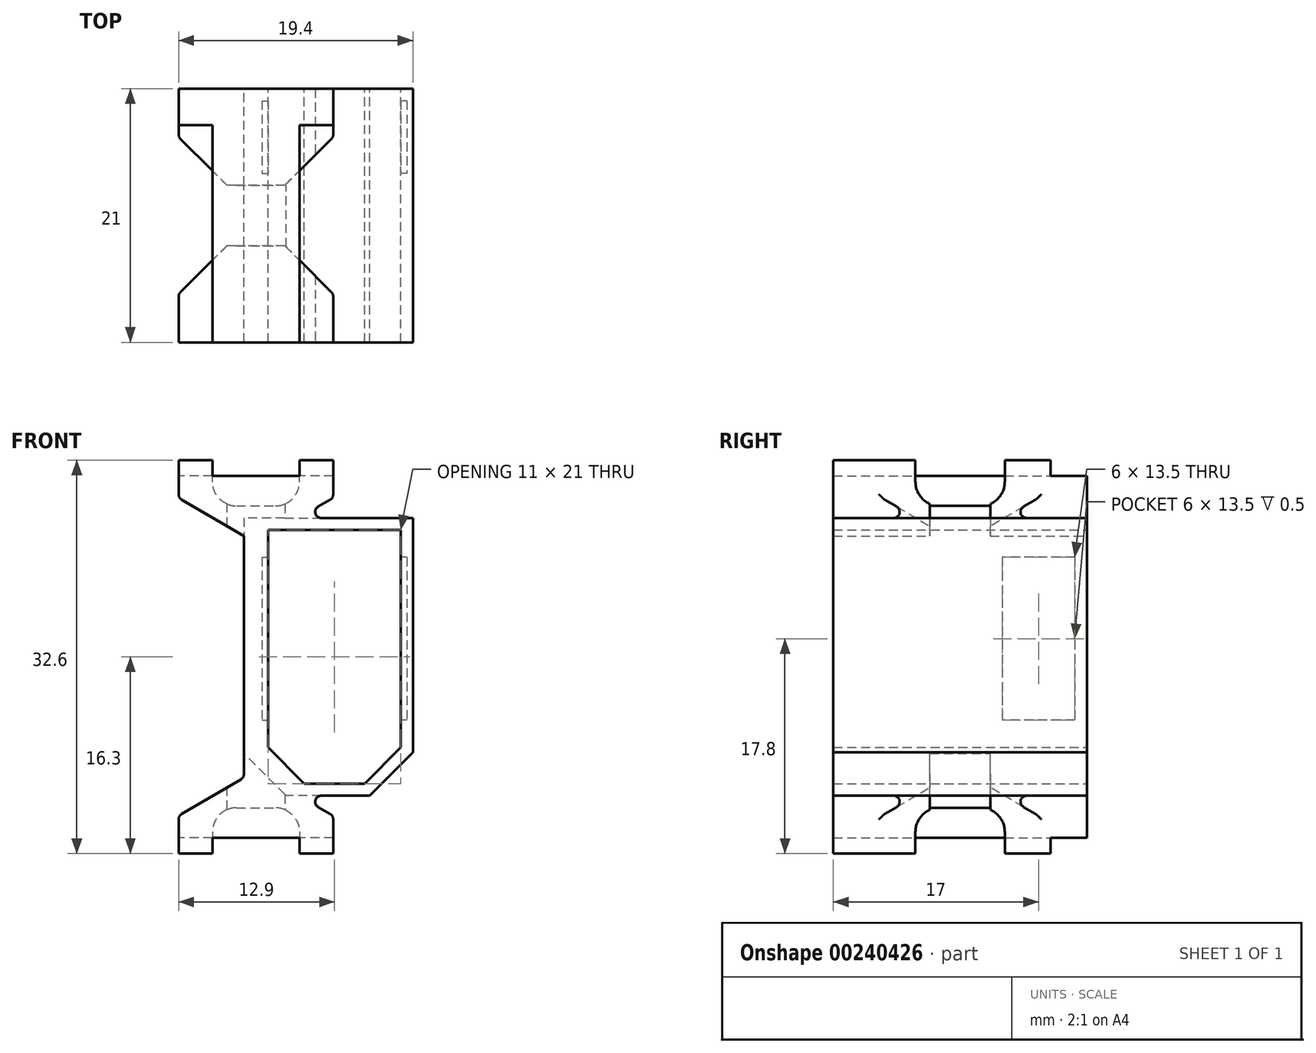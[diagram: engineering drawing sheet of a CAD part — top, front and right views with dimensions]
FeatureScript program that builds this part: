
annotation { "Feature Type Name" : "Feature", "Feature Type Description" : "" }
export const myFeature = defineFeature(function(context is Context, id is Id, definition is map)
    precondition{}
    {
        {
            var Q0;
            Q0=qCreatedBy(makeId("Front.planeOp"),FACE);
            var sketch = newSketch(context, id + "F0", { "sketchPlane" : qUnion([Q0])});
            skLineSegment(sketch, "E0", {"start": v(-1, 10) * mm, "end": v(-1, -10) * mm});
            skLineSegment(sketch, "E1", {"start": v(-6.4, 16.3) * mm, "end": v(-6.4, 13.16) * mm});
            skLineSegment(sketch, "E2", {"start": v(-6.4, 16.3) * mm, "end": v(-3.6, 16.3) * mm});
            skLineSegment(sketch, "E3", {"start": v(-3.6, 16.3) * mm, "end": v(-3.6, 15) * mm});
            skLineSegment(sketch, "E4", {"start": v(-3.6, 15) * mm, "end": v(0, 15) * mm});
            skLineSegment(sketch, "E5", {"start": v(-6.4, 13.16) * mm, "end": v(-1, 10) * mm});
            skLineSegment(sketch, "E6.MirrorCS", {"start": v(-3.6, -16.3) * mm, "end": v(-3.6, -15) * mm});
            skLineSegment(sketch, "E7.MirrorCS", {"start": v(-6.4, -13.16) * mm, "end": v(-1, -10) * mm});
            skLineSegment(sketch, "E8.MirrorCS", {"start": v(-3.6, -15) * mm, "end": v(0, -15) * mm});
            skLineSegment(sketch, "E9.MirrorCS", {"start": v(-6.4, -16.3) * mm, "end": v(-6.4, -13.16) * mm});
            skLineSegment(sketch, "E10.MirrorCS", {"start": v(-6.4, -16.3) * mm, "end": v(-3.6, -16.3) * mm});
            skLineSegment(sketch, "E11.MirrorCS", {"start": v(3.6, -16.3) * mm, "end": v(3.6, -15) * mm});
            skLineSegment(sketch, "E12.MirrorCS", {"start": v(3.6, 16.3) * mm, "end": v(3.6, 15) * mm});
            skLineSegment(sketch, "E13.MirrorCS", {"start": v(6.4, -16.3) * mm, "end": v(3.6, -16.3) * mm});
            skLineSegment(sketch, "E14.MirrorCS", {"start": v(6.4, -16.3) * mm, "end": v(6.4, -13.16) * mm});
            skLineSegment(sketch, "E15.MirrorCS", {"start": v(3.6, -15) * mm, "end": v(0, -15) * mm});
            skLineSegment(sketch, "E16.MirrorCS", {"start": v(6.4, -13.16) * mm, "end": v(1, -10) * mm});
            skLineSegment(sketch, "E17.MirrorCS", {"start": v(6.4, 16.3) * mm, "end": v(3.6, 16.3) * mm});
            skLineSegment(sketch, "E18.MirrorCS", {"start": v(1, 10) * mm, "end": v(1, -10) * mm});
            skLineSegment(sketch, "E19.MirrorCS", {"start": v(6.4, 16.3) * mm, "end": v(6.4, 13.16) * mm});
            skLineSegment(sketch, "E20.MirrorCS", {"start": v(6.4, 13.16) * mm, "end": v(1, 10) * mm});
            skLineSegment(sketch, "E21.MirrorCS", {"start": v(3.6, 15) * mm, "end": v(0, 15) * mm});
            skPoint(sketch, "E22", {"position": v(-5, 16.3) * mm});
            skPoint(sketch, "E23", {"position": v(5, 16.3) * mm});
            skLineSegment(sketch, "E24", {"start": v(-3.6, 15) * mm, "end": v(-5.12, 12.41) * mm, "construction": true});
            skSolve(sketch);
        }
        {
            var Q0;
            Q0 = qSketchRegion(id + "F0", true);
            extrude(context, id + "F1", {"entities" : qUnion([Q0]), "depth" : 21 * mm});
        }
        {
            var Q0;
            Q0=makeQuery(id+"F1.opExtrude","SWEPT_EDGE",EDGE,{"disambiguationData":[OSD([sQuery(id+"F0.wireOp",EDGE,"E1"),sQuery(id+"F0.wireOp",EDGE,"E2")])]});
            cPoint(context, id + "F2", {"entities" : qUnion([Q0]), "parameter" : 0.5});
        }
        {
            var Q0;
            Q0=makeQuery(id+"F1.opExtrude","SWEPT_EDGE",EDGE,{"disambiguationData":[OSD([sQuery(id+"F0.wireOp",EDGE,"E9.MirrorCS"),sQuery(id+"F0.wireOp",EDGE,"E10.MirrorCS")])]});
            cPoint(context, id + "F3", {"entities" : qUnion([Q0]), "parameter" : 0.5});
        }
        {
            var Q0;
            Q0=makeQuery(id+"F1.opExtrude","SWEPT_EDGE",EDGE,{"disambiguationData":[OSD([sQuery(id+"F0.wireOp",EDGE,"E13.MirrorCS"),sQuery(id+"F0.wireOp",EDGE,"E14.MirrorCS")])]});
            cPoint(context, id + "F4", {"entities" : qUnion([Q0]), "parameter" : 0.5});
        }
        {
            var Q0;
            Q0 = qCreatedBy(id + "F2" ,VERTEX);
            var Q1;
            Q1 = qCreatedBy(id + "F3" ,VERTEX);
            var Q2;
            Q2 = qCreatedBy(id + "F4" ,VERTEX);
            cPlane(context, id + "F5", {"entities" : qUnion([Q0, Q1, Q2]), "cplaneType" : CPlaneType.THREE_POINT, "offset" : 25 * mm, "width" : 150 * mm, "height" : 150 * mm});
        }
        {
            var Q0;
            Q0=qCreatedBy(id+"F5.planeOp",FACE);
            var sketch = newSketch(context, id + "F6", { "sketchPlane" : qUnion([Q0])});
            skLineSegment(sketch, "E25.bottom", {"start": v(20, 25) * mm, "end": v(3.6, 25) * mm});
            skLineSegment(sketch, "E25.top", {"start": v(20, -25) * mm, "end": v(3.6, -25) * mm});
            skLineSegment(sketch, "E25.left", {"start": v(20, 25) * mm, "end": v(20, -25) * mm});
            skLineSegment(sketch, "E25.right", {"start": v(3.6, 25) * mm, "end": v(3.6, 12.5) * mm});
            skLineSegment(sketch, "E26.MirrorCS", {"start": v(-3.6, 25) * mm, "end": v(-3.6, 12.5) * mm});
            skLineSegment(sketch, "E27.MirrorCS", {"start": v(-20, 25) * mm, "end": v(-20, -25) * mm});
            skLineSegment(sketch, "E28.MirrorCS", {"start": v(-20, 25) * mm, "end": v(-3.6, 25) * mm});
            skLineSegment(sketch, "E29.MirrorCS", {"start": v(-20, -25) * mm, "end": v(-3.6, -25) * mm});
            skLineSegment(sketch, "E30.bottom", {"start": v(3.6, 12.5) * mm, "end": v(-3.6, 12.5) * mm});
            skLineSegment(sketch, "E30.top", {"start": v(3.6, -12.5) * mm, "end": v(-3.6, -12.5) * mm});
            skLineSegment(sketch, "E31.trimOffspring", {"start": v(-3.6, -12.5) * mm, "end": v(-3.6, -25) * mm});
            skLineSegment(sketch, "E32.trimOffspring", {"start": v(3.6, -12.5) * mm, "end": v(3.6, -25) * mm});
            skSolve(sketch);
        }
        {
            var Q0;
            Q0 = qSketchRegion(id + "F6", true);
            extrude(context, id + "F7", {"entities" : qUnion([Q0]), "operationType" : NewBodyOperationType.REMOVE, "oppositeDirection" : true, "depth" : 2.5 * mm, "hasSecondDirection" : true, "secondDirectionOppositeDirection" : false, "secondDirectionDepth" : 2.5 * mm});
        }
        {
            var Q0;
            Q0=makeQuery(id+"F7.boolean.opBoolean","INTERSECT",EDGE,{"derivedFrom":[makeQuery(id+"F1.opExtrude","SWEPT_FACE",FACE,{"disambiguationData":[OSD([sQuery(id+"F0.wireOp",EDGE,"E1")])]}),makeQuery(id+"F7.opExtrude","CAP_FACE",FACE,{"disambiguationData":[OSD([sQuery(id+"F6.wireOp",EDGE,"E25.bottom"),sQuery(id+"F6.wireOp",EDGE,"E25.top"),sQuery(id+"F6.wireOp",EDGE,"E25.left"),sQuery(id+"F6.wireOp",EDGE,"E25.right"),sQuery(id+"F6.wireOp",EDGE,"E26.MirrorCS"),sQuery(id+"F6.wireOp",EDGE,"E27.MirrorCS"),sQuery(id+"F6.wireOp",EDGE,"E28.MirrorCS"),sQuery(id+"F6.wireOp",EDGE,"E29.MirrorCS"),sQuery(id+"F6.wireOp",EDGE,"E30.bottom"),sQuery(id+"F6.wireOp",EDGE,"E30.top"),sQuery(id+"F6.wireOp",EDGE,"E31.trimOffspring"),sQuery(id+"F6.wireOp",EDGE,"E32.trimOffspring")])],"isStart":true})]});
            var Q1;
            Q1=makeQuery(id+"F7.boolean.opBoolean","INTERSECT",EDGE,{"derivedFrom":[makeQuery(id+"F1.opExtrude","SWEPT_FACE",FACE,{"disambiguationData":[OSD([sQuery(id+"F0.wireOp",EDGE,"E1")])]}),makeQuery(id+"F7.opExtrude","CAP_FACE",FACE,{"disambiguationData":[OSD([sQuery(id+"F6.wireOp",EDGE,"E25.bottom"),sQuery(id+"F6.wireOp",EDGE,"E25.top"),sQuery(id+"F6.wireOp",EDGE,"E25.left"),sQuery(id+"F6.wireOp",EDGE,"E25.right"),sQuery(id+"F6.wireOp",EDGE,"E26.MirrorCS"),sQuery(id+"F6.wireOp",EDGE,"E27.MirrorCS"),sQuery(id+"F6.wireOp",EDGE,"E28.MirrorCS"),sQuery(id+"F6.wireOp",EDGE,"E29.MirrorCS"),sQuery(id+"F6.wireOp",EDGE,"E30.bottom"),sQuery(id+"F6.wireOp",EDGE,"E30.top"),sQuery(id+"F6.wireOp",EDGE,"E31.trimOffspring"),sQuery(id+"F6.wireOp",EDGE,"E32.trimOffspring")])],"isStart":false})]});
            var Q2;
            Q2=makeQuery(id+"F7.boolean.opBoolean","INTERSECT",EDGE,{"derivedFrom":[makeQuery(id+"F1.opExtrude","SWEPT_FACE",FACE,{"disambiguationData":[OSD([sQuery(id+"F0.wireOp",EDGE,"E19.MirrorCS")])]}),makeQuery(id+"F7.opExtrude","CAP_FACE",FACE,{"disambiguationData":[OSD([sQuery(id+"F6.wireOp",EDGE,"E25.bottom"),sQuery(id+"F6.wireOp",EDGE,"E25.top"),sQuery(id+"F6.wireOp",EDGE,"E25.left"),sQuery(id+"F6.wireOp",EDGE,"E25.right"),sQuery(id+"F6.wireOp",EDGE,"E26.MirrorCS"),sQuery(id+"F6.wireOp",EDGE,"E27.MirrorCS"),sQuery(id+"F6.wireOp",EDGE,"E28.MirrorCS"),sQuery(id+"F6.wireOp",EDGE,"E29.MirrorCS"),sQuery(id+"F6.wireOp",EDGE,"E30.bottom"),sQuery(id+"F6.wireOp",EDGE,"E30.top"),sQuery(id+"F6.wireOp",EDGE,"E31.trimOffspring"),sQuery(id+"F6.wireOp",EDGE,"E32.trimOffspring")])],"isStart":false})]});
            var Q3;
            Q3=makeQuery(id+"F7.boolean.opBoolean","INTERSECT",EDGE,{"derivedFrom":[makeQuery(id+"F1.opExtrude","SWEPT_FACE",FACE,{"disambiguationData":[OSD([sQuery(id+"F0.wireOp",EDGE,"E19.MirrorCS")])]}),makeQuery(id+"F7.opExtrude","CAP_FACE",FACE,{"disambiguationData":[OSD([sQuery(id+"F6.wireOp",EDGE,"E25.bottom"),sQuery(id+"F6.wireOp",EDGE,"E25.top"),sQuery(id+"F6.wireOp",EDGE,"E25.left"),sQuery(id+"F6.wireOp",EDGE,"E25.right"),sQuery(id+"F6.wireOp",EDGE,"E26.MirrorCS"),sQuery(id+"F6.wireOp",EDGE,"E27.MirrorCS"),sQuery(id+"F6.wireOp",EDGE,"E28.MirrorCS"),sQuery(id+"F6.wireOp",EDGE,"E29.MirrorCS"),sQuery(id+"F6.wireOp",EDGE,"E30.bottom"),sQuery(id+"F6.wireOp",EDGE,"E30.top"),sQuery(id+"F6.wireOp",EDGE,"E31.trimOffspring"),sQuery(id+"F6.wireOp",EDGE,"E32.trimOffspring")])],"isStart":true})]});
            var Q4;
            Q4=makeQuery(id+"F7.boolean.opBoolean","INTERSECT",EDGE,{"derivedFrom":[makeQuery(id+"F1.opExtrude","SWEPT_FACE",FACE,{"disambiguationData":[OSD([sQuery(id+"F0.wireOp",EDGE,"E9.MirrorCS")])]}),makeQuery(id+"F7.opExtrude","CAP_FACE",FACE,{"disambiguationData":[OSD([sQuery(id+"F6.wireOp",EDGE,"E25.bottom"),sQuery(id+"F6.wireOp",EDGE,"E25.top"),sQuery(id+"F6.wireOp",EDGE,"E25.left"),sQuery(id+"F6.wireOp",EDGE,"E25.right"),sQuery(id+"F6.wireOp",EDGE,"E26.MirrorCS"),sQuery(id+"F6.wireOp",EDGE,"E27.MirrorCS"),sQuery(id+"F6.wireOp",EDGE,"E28.MirrorCS"),sQuery(id+"F6.wireOp",EDGE,"E29.MirrorCS"),sQuery(id+"F6.wireOp",EDGE,"E30.bottom"),sQuery(id+"F6.wireOp",EDGE,"E30.top"),sQuery(id+"F6.wireOp",EDGE,"E31.trimOffspring"),sQuery(id+"F6.wireOp",EDGE,"E32.trimOffspring")])],"isStart":true})]});
            var Q5;
            Q5=makeQuery(id+"F7.boolean.opBoolean","INTERSECT",EDGE,{"derivedFrom":[makeQuery(id+"F1.opExtrude","SWEPT_FACE",FACE,{"disambiguationData":[OSD([sQuery(id+"F0.wireOp",EDGE,"E9.MirrorCS")])]}),makeQuery(id+"F7.opExtrude","CAP_FACE",FACE,{"disambiguationData":[OSD([sQuery(id+"F6.wireOp",EDGE,"E25.bottom"),sQuery(id+"F6.wireOp",EDGE,"E25.top"),sQuery(id+"F6.wireOp",EDGE,"E25.left"),sQuery(id+"F6.wireOp",EDGE,"E25.right"),sQuery(id+"F6.wireOp",EDGE,"E26.MirrorCS"),sQuery(id+"F6.wireOp",EDGE,"E27.MirrorCS"),sQuery(id+"F6.wireOp",EDGE,"E28.MirrorCS"),sQuery(id+"F6.wireOp",EDGE,"E29.MirrorCS"),sQuery(id+"F6.wireOp",EDGE,"E30.bottom"),sQuery(id+"F6.wireOp",EDGE,"E30.top"),sQuery(id+"F6.wireOp",EDGE,"E31.trimOffspring"),sQuery(id+"F6.wireOp",EDGE,"E32.trimOffspring")])],"isStart":false})]});
            var Q6;
            Q6=makeQuery(id+"F7.boolean.opBoolean","INTERSECT",EDGE,{"derivedFrom":[makeQuery(id+"F1.opExtrude","SWEPT_FACE",FACE,{"disambiguationData":[OSD([sQuery(id+"F0.wireOp",EDGE,"E14.MirrorCS")])]}),makeQuery(id+"F7.opExtrude","CAP_FACE",FACE,{"disambiguationData":[OSD([sQuery(id+"F6.wireOp",EDGE,"E25.bottom"),sQuery(id+"F6.wireOp",EDGE,"E25.top"),sQuery(id+"F6.wireOp",EDGE,"E25.left"),sQuery(id+"F6.wireOp",EDGE,"E25.right"),sQuery(id+"F6.wireOp",EDGE,"E26.MirrorCS"),sQuery(id+"F6.wireOp",EDGE,"E27.MirrorCS"),sQuery(id+"F6.wireOp",EDGE,"E28.MirrorCS"),sQuery(id+"F6.wireOp",EDGE,"E29.MirrorCS"),sQuery(id+"F6.wireOp",EDGE,"E30.bottom"),sQuery(id+"F6.wireOp",EDGE,"E30.top"),sQuery(id+"F6.wireOp",EDGE,"E31.trimOffspring"),sQuery(id+"F6.wireOp",EDGE,"E32.trimOffspring")])],"isStart":false})]});
            var Q7;
            Q7=makeQuery(id+"F7.boolean.opBoolean","INTERSECT",EDGE,{"derivedFrom":[makeQuery(id+"F1.opExtrude","SWEPT_FACE",FACE,{"disambiguationData":[OSD([sQuery(id+"F0.wireOp",EDGE,"E14.MirrorCS")])]}),makeQuery(id+"F7.opExtrude","CAP_FACE",FACE,{"disambiguationData":[OSD([sQuery(id+"F6.wireOp",EDGE,"E25.bottom"),sQuery(id+"F6.wireOp",EDGE,"E25.top"),sQuery(id+"F6.wireOp",EDGE,"E25.left"),sQuery(id+"F6.wireOp",EDGE,"E25.right"),sQuery(id+"F6.wireOp",EDGE,"E26.MirrorCS"),sQuery(id+"F6.wireOp",EDGE,"E27.MirrorCS"),sQuery(id+"F6.wireOp",EDGE,"E28.MirrorCS"),sQuery(id+"F6.wireOp",EDGE,"E29.MirrorCS"),sQuery(id+"F6.wireOp",EDGE,"E30.bottom"),sQuery(id+"F6.wireOp",EDGE,"E30.top"),sQuery(id+"F6.wireOp",EDGE,"E31.trimOffspring"),sQuery(id+"F6.wireOp",EDGE,"E32.trimOffspring")])],"isStart":true})]});
            chamfer(context, id + "F8", {"entities" : qUnion([Q0, Q1, Q2, Q3, Q4, Q5, Q6, Q7]), "width" : 4 * mm, "tangentPropagation" : true});
        }
        {
            var Q0;
            Q0=qCreatedBy(id+"F5.planeOp",FACE);
            var sketch = newSketch(context, id + "F9", { "sketchPlane" : qUnion([Q0])});
            skLineSegment(sketch, "E33", {"start": v(-12, 10.5) * mm, "end": v(-1, 10.5) * mm});
            skLineSegment(sketch, "E34", {"start": v(-1, 10.5) * mm, "end": v(-1, -7.5) * mm});
            skLineSegment(sketch, "E35", {"start": v(-6.5, 10.5) * mm, "end": v(-6.5, -10.5) * mm, "construction": true});
            skLineSegment(sketch, "E36", {"start": v(-1, -7.5) * mm, "end": v(-4, -10.5) * mm});
            skLineSegment(sketch, "E37.MirrorCS", {"start": v(-12, -7.5) * mm, "end": v(-9, -10.5) * mm});
            skLineSegment(sketch, "E38.MirrorCS", {"start": v(-12, 10.5) * mm, "end": v(-12, -7.5) * mm});
            skLineSegment(sketch, "E39", {"start": v(-9, -10.5) * mm, "end": v(-4, -10.5) * mm});
            skLineSegment(sketch, "E40.0", {"start": v(-13, 11.5) * mm, "end": v(1, 11.5) * mm});
            skLineSegment(sketch, "E40.2", {"start": v(-9.41, -11.5) * mm, "end": v(-4.09, -11.5) * mm});
            skLineSegment(sketch, "E40.3", {"start": v(-13, -7.91) * mm, "end": v(-9.41, -11.5) * mm});
            skLineSegment(sketch, "E40.4", {"start": v(-13, 11.5) * mm, "end": v(-13, -7.91) * mm});
            skLineSegment(sketch, "E41", {"start": v(1, 11.5) * mm, "end": v(1, -8) * mm});
            skLineSegment(sketch, "E42", {"start": v(-4.09, -11.5) * mm, "end": v(-2.5, -11.5) * mm});
            skLineSegment(sketch, "E43", {"start": v(-2.5, -11.5) * mm, "end": v(1, -8) * mm});
            skSolve(sketch);
        }
        {
            var Q0;
            Q0 = qSketchRegion(id + "F9", true);
            var Q1;
            Q1=makeQuery(id+"F1.opExtrude","CAP_FACE",FACE,{"disambiguationData":[OSD([sQuery(id+"F0.wireOp",EDGE,"E0"),sQuery(id+"F0.wireOp",EDGE,"E1"),sQuery(id+"F0.wireOp",EDGE,"E2"),sQuery(id+"F0.wireOp",EDGE,"E3"),sQuery(id+"F0.wireOp",EDGE,"E4"),sQuery(id+"F0.wireOp",EDGE,"E5"),sQuery(id+"F0.wireOp",EDGE,"E6.MirrorCS"),sQuery(id+"F0.wireOp",EDGE,"E7.MirrorCS"),sQuery(id+"F0.wireOp",EDGE,"E8.MirrorCS"),sQuery(id+"F0.wireOp",EDGE,"E9.MirrorCS"),sQuery(id+"F0.wireOp",EDGE,"E10.MirrorCS"),sQuery(id+"F0.wireOp",EDGE,"E11.MirrorCS"),sQuery(id+"F0.wireOp",EDGE,"E12.MirrorCS"),sQuery(id+"F0.wireOp",EDGE,"E13.MirrorCS"),sQuery(id+"F0.wireOp",EDGE,"E14.MirrorCS"),sQuery(id+"F0.wireOp",EDGE,"E15.MirrorCS"),sQuery(id+"F0.wireOp",EDGE,"E16.MirrorCS"),sQuery(id+"F0.wireOp",EDGE,"E17.MirrorCS"),sQuery(id+"F0.wireOp",EDGE,"E18.MirrorCS"),sQuery(id+"F0.wireOp",EDGE,"E19.MirrorCS"),sQuery(id+"F0.wireOp",EDGE,"E20.MirrorCS"),sQuery(id+"F0.wireOp",EDGE,"E21.MirrorCS")])],"isStart":false});
            var Q2;
            Q2=makeQuery(id+"F1.opExtrude","CAP_FACE",FACE,{"disambiguationData":[OSD([sQuery(id+"F0.wireOp",EDGE,"E0"),sQuery(id+"F0.wireOp",EDGE,"E1"),sQuery(id+"F0.wireOp",EDGE,"E2"),sQuery(id+"F0.wireOp",EDGE,"E3"),sQuery(id+"F0.wireOp",EDGE,"E4"),sQuery(id+"F0.wireOp",EDGE,"E5"),sQuery(id+"F0.wireOp",EDGE,"E6.MirrorCS"),sQuery(id+"F0.wireOp",EDGE,"E7.MirrorCS"),sQuery(id+"F0.wireOp",EDGE,"E8.MirrorCS"),sQuery(id+"F0.wireOp",EDGE,"E9.MirrorCS"),sQuery(id+"F0.wireOp",EDGE,"E10.MirrorCS"),sQuery(id+"F0.wireOp",EDGE,"E11.MirrorCS"),sQuery(id+"F0.wireOp",EDGE,"E12.MirrorCS"),sQuery(id+"F0.wireOp",EDGE,"E13.MirrorCS"),sQuery(id+"F0.wireOp",EDGE,"E14.MirrorCS"),sQuery(id+"F0.wireOp",EDGE,"E15.MirrorCS"),sQuery(id+"F0.wireOp",EDGE,"E16.MirrorCS"),sQuery(id+"F0.wireOp",EDGE,"E17.MirrorCS"),sQuery(id+"F0.wireOp",EDGE,"E18.MirrorCS"),sQuery(id+"F0.wireOp",EDGE,"E19.MirrorCS"),sQuery(id+"F0.wireOp",EDGE,"E20.MirrorCS"),sQuery(id+"F0.wireOp",EDGE,"E21.MirrorCS")])],"isStart":true});
            extrude(context, id + "F10", {"entities" : qUnion([Q0]), "operationType" : NewBodyOperationType.ADD, "endBound" : BoundingType.UP_TO_SURFACE, "oppositeDirection" : true, "endBoundEntityFace" : qUnion([Q1]), "depth" : 25 * mm, "hasSecondDirection" : true, "secondDirectionBound" : BoundingType.UP_TO_SURFACE, "secondDirectionOppositeDirection" : false, "secondDirectionBoundEntityFace" : qUnion([Q2]), "secondDirectionDepth" : 25 * mm});
        }
        {
            var Q0;
            Q0=makeQuery(id+"F9.imprint","IMPRINT",FACE,{"disambiguationData":[TD([[makeQuery(id+"F9.imprint","IMPRINT",EDGE,{"derivedFrom":sQuery(id+"F9.wireOp",EDGE,"E33")}),-1.0]])]});
            extrude(context, id + "F11", {"entities" : qUnion([Q0]), "operationType" : NewBodyOperationType.REMOVE, "endBound" : BoundingType.THROUGH_ALL, "oppositeDirection" : true, "depth" : 25 * mm, "hasSecondDirection" : true, "secondDirectionBound" : BoundingType.THROUGH_ALL, "secondDirectionOppositeDirection" : false, "secondDirectionDepth" : 25 * mm});
        }
        {
            var Q0;
            {var subQ0=sQuery(id+"F9.wireOp",EDGE,"E34");var subQ4=sQuery(id+"F0.wireOp",EDGE,"E18.MirrorCS");var subQ25=sQuery(id+"F6.wireOp",EDGE,"E32.trimOffspring");var subQ26=sQuery(id+"F6.wireOp",EDGE,"E31.trimOffspring");var subQ27=sQuery(id+"F6.wireOp",EDGE,"E30.top");var subQ28=sQuery(id+"F6.wireOp",EDGE,"E30.bottom");var subQ29=sQuery(id+"F6.wireOp",EDGE,"E29.MirrorCS");var subQ30=sQuery(id+"F6.wireOp",EDGE,"E28.MirrorCS");var subQ31=sQuery(id+"F6.wireOp",EDGE,"E27.MirrorCS");var subQ32=sQuery(id+"F6.wireOp",EDGE,"E26.MirrorCS");var subQ33=sQuery(id+"F6.wireOp",EDGE,"E25.right");var subQ34=sQuery(id+"F6.wireOp",EDGE,"E25.left");var subQ35=sQuery(id+"F6.wireOp",EDGE,"E25.top");var subQ36=sQuery(id+"F6.wireOp",EDGE,"E25.bottom");var subQ37=makeQuery(id+"F1.opExtrude","SWEPT_FACE",FACE,{"disambiguationData":[OSD([subQ4])]});Q0=makeQuery(id+"F11.boolean.opBoolean","MERGE",FACE,{"derivedFrom":[makeQuery(id+"F10.boolean.opBoolean","MERGE",FACE,{"derivedFrom":[makeQuery(id+"F7.boolean.opBoolean","SPLIT",FACE,{"disambiguationData":[TD([makeQuery(id+"F7.opExtrude","CAP_FACE",FACE,{"disambiguationData":[OSD([subQ36,subQ35,subQ34,subQ33,subQ32,subQ31,subQ30,subQ29,subQ28,subQ27,subQ26,subQ25])],"isStart":true})])],"derivedFrom":subQ37}),makeQuery(id+"F7.boolean.opBoolean","SPLIT",FACE,{"disambiguationData":[TD([makeQuery(id+"F7.opExtrude","CAP_FACE",FACE,{"disambiguationData":[OSD([subQ36,subQ35,subQ34,subQ33,subQ32,subQ31,subQ30,subQ29,subQ28,subQ27,subQ26,subQ25])],"isStart":false})])],"derivedFrom":subQ37}),makeQuery(id+"F10.opExtrude","SWEPT_FACE",FACE,{"disambiguationData":[OSD([subQ0])]})]})],"fromTools":[makeQuery(id+"F11.opExtrude","SWEPT_FACE",FACE,{"disambiguationData":[OSD([subQ0])]})]});}
            var sketch = newSketch(context, id + "F12", { "sketchPlane" : qUnion([Q0])});
            skLineSegment(sketch, "E44.bottom", {"start": v(-1, 8.25) * mm, "end": v(-7, 8.25) * mm});
            skLineSegment(sketch, "E44.top", {"start": v(-1, -5.25) * mm, "end": v(-7, -5.25) * mm});
            skLineSegment(sketch, "E44.left", {"start": v(-1, 8.25) * mm, "end": v(-1, -5.25) * mm});
            skLineSegment(sketch, "E44.right", {"start": v(-7, 8.25) * mm, "end": v(-7, -5.25) * mm});
            skLineSegment(sketch, "E45", {"start": v(-7, 1.5) * mm, "end": v(-1, 1.5) * mm, "construction": true});
            skSolve(sketch);
        }
        {
            var Q0;
            Q0 = qSketchRegion(id + "F12", true);
            extrude(context, id + "F13", {"entities" : qUnion([Q0]), "oppositeDirection" : true, "depth" : 0.5 * mm});
        }
        {
            var Q0;
            Q0=makeQuery(id+"F10.opExtrude","CAP_EDGE",EDGE,{"disambiguationData":[OSD([sQuery(id+"F9.wireOp",EDGE,"E39")])],"isStart":true});
            cPoint(context, id + "F14", {"entities" : qUnion([Q0]), "parameter" : 0.5});
        }
        {
            var Q0;
            Q0=sQuery(id+"F9.wireOp",VERTEX,"E35.start");
            var Q1;
            Q1=sQuery(id+"F9.wireOp",VERTEX,"E35.end");
            var Q2;
            Q2 = qCreatedBy(id + "F14" ,VERTEX);
            cPlane(context, id + "F15", {"entities" : qUnion([Q0, Q1, Q2]), "cplaneType" : CPlaneType.THREE_POINT, "offset" : 25 * mm, "flipAlignment" : true, "width" : 150 * mm, "height" : 150 * mm});
        }
        {
            var Q0;
            Q0=makeQuery(id+"F13.opExtrude","SWEPT_BODY",BODY,{"disambiguationData":[OSD([sQuery(id+"F12.wireOp",EDGE,"E44.bottom"),sQuery(id+"F12.wireOp",EDGE,"E44.top"),sQuery(id+"F12.wireOp",EDGE,"E44.left"),sQuery(id+"F12.wireOp",EDGE,"E44.right")])]});
            var Q1;
            Q1=qCreatedBy(id+"F15.planeOp",FACE);
            mirror(context, id + "F16", {"operationType" : NewBodyOperationType.REMOVE, "entities" : qUnion([Q0]), "mirrorPlane" : qUnion([Q1])});
        }
        {
            var Q0;
            Q0=makeQuery(id+"F13.opExtrude","SWEPT_BODY",BODY,{"disambiguationData":[OSD([sQuery(id+"F12.wireOp",EDGE,"E44.bottom"),sQuery(id+"F12.wireOp",EDGE,"E44.top"),sQuery(id+"F12.wireOp",EDGE,"E44.left"),sQuery(id+"F12.wireOp",EDGE,"E44.right")])]});
            var Q1;
            Q1=makeQuery(id+"F1.opExtrude","SWEPT_BODY",BODY,{"disambiguationData":[OSD([sQuery(id+"F0.wireOp",EDGE,"E0"),sQuery(id+"F0.wireOp",EDGE,"E1"),sQuery(id+"F0.wireOp",EDGE,"E2"),sQuery(id+"F0.wireOp",EDGE,"E3"),sQuery(id+"F0.wireOp",EDGE,"E4"),sQuery(id+"F0.wireOp",EDGE,"E5"),sQuery(id+"F0.wireOp",EDGE,"E6.MirrorCS"),sQuery(id+"F0.wireOp",EDGE,"E7.MirrorCS"),sQuery(id+"F0.wireOp",EDGE,"E8.MirrorCS"),sQuery(id+"F0.wireOp",EDGE,"E9.MirrorCS"),sQuery(id+"F0.wireOp",EDGE,"E10.MirrorCS"),sQuery(id+"F0.wireOp",EDGE,"E11.MirrorCS"),sQuery(id+"F0.wireOp",EDGE,"E12.MirrorCS"),sQuery(id+"F0.wireOp",EDGE,"E13.MirrorCS"),sQuery(id+"F0.wireOp",EDGE,"E14.MirrorCS"),sQuery(id+"F0.wireOp",EDGE,"E15.MirrorCS"),sQuery(id+"F0.wireOp",EDGE,"E16.MirrorCS"),sQuery(id+"F0.wireOp",EDGE,"E17.MirrorCS"),sQuery(id+"F0.wireOp",EDGE,"E18.MirrorCS"),sQuery(id+"F0.wireOp",EDGE,"E19.MirrorCS"),sQuery(id+"F0.wireOp",EDGE,"E20.MirrorCS"),sQuery(id+"F0.wireOp",EDGE,"E21.MirrorCS")])]});
            booleanBodies(context, id + "F17", {"operationType" : BooleanOperationType.SUBTRACTION, "tools" : qUnion([Q0]), "targets" : qUnion([Q1])});
        }
        {
            var Q0;
            Q0=makeQuery(id+"F7.boolean.opBoolean","COPY",EDGE,{"derivedFrom":makeQuery(id+"F7.opExtrude","SWEPT_EDGE",EDGE,{"disambiguationData":[OSD([sQuery(id+"F6.wireOp",EDGE,"E26.MirrorCS"),sQuery(id+"F6.wireOp",EDGE,"E30.bottom")])]})});
            var Q1;
            Q1=makeQuery(id+"F7.boolean.opBoolean","COPY",EDGE,{"derivedFrom":makeQuery(id+"F7.opExtrude","SWEPT_EDGE",EDGE,{"disambiguationData":[OSD([sQuery(id+"F6.wireOp",EDGE,"E25.right"),sQuery(id+"F6.wireOp",EDGE,"E30.bottom")])]})});
            var Q2;
            Q2=makeQuery(id+"F7.boolean.opBoolean","COPY",EDGE,{"derivedFrom":makeQuery(id+"F7.opExtrude","SWEPT_EDGE",EDGE,{"disambiguationData":[OSD([sQuery(id+"F6.wireOp",EDGE,"E30.top"),sQuery(id+"F6.wireOp",EDGE,"E32.trimOffspring")])]})});
            var Q3;
            Q3=makeQuery(id+"F7.boolean.opBoolean","COPY",EDGE,{"derivedFrom":makeQuery(id+"F7.opExtrude","SWEPT_EDGE",EDGE,{"disambiguationData":[OSD([sQuery(id+"F6.wireOp",EDGE,"E30.top"),sQuery(id+"F6.wireOp",EDGE,"E31.trimOffspring")])]})});
            var Q4;
            Q4=makeQuery(id+"F10.opExtrude","TWEAK_EDGE",EDGE,{"derivedFrom":[makeQuery(id+"F9.imprint","IMPRINT",EDGE,{"derivedFrom":sQuery(id+"F9.wireOp",EDGE,"E40.0")}),makeQuery(id+"F9.imprint","IMPRINT",EDGE,{"derivedFrom":sQuery(id+"F9.wireOp",EDGE,"E41")})]});
            var Q5;
            Q5=makeQuery(id+"F10.opExtrude","TWEAK_EDGE",EDGE,{"derivedFrom":[makeQuery(id+"F9.imprint","IMPRINT",EDGE,{"derivedFrom":sQuery(id+"F9.wireOp",EDGE,"E41")}),makeQuery(id+"F9.imprint","IMPRINT",EDGE,{"derivedFrom":sQuery(id+"F9.wireOp",EDGE,"E43")})]});
            fillet(context, id + "F18", {"entities" : qUnion([Q0, Q1, Q2, Q3, Q4, Q5]), "radius" : 2 * mm, "tangentPropagation" : true, "allowEdgeOverflow" : false});
        }
        {
            var Q0;
            {var subQ2=sQuery(id+"F0.wireOp",EDGE,"E1");var subQ3=makeQuery(id+"F7.opExtrude","CAP_FACE",FACE,{"disambiguationData":[OSD([sQuery(id+"F6.wireOp",EDGE,"E25.bottom"),sQuery(id+"F6.wireOp",EDGE,"E25.top"),sQuery(id+"F6.wireOp",EDGE,"E25.left"),sQuery(id+"F6.wireOp",EDGE,"E25.right"),sQuery(id+"F6.wireOp",EDGE,"E26.MirrorCS"),sQuery(id+"F6.wireOp",EDGE,"E27.MirrorCS"),sQuery(id+"F6.wireOp",EDGE,"E28.MirrorCS"),sQuery(id+"F6.wireOp",EDGE,"E29.MirrorCS"),sQuery(id+"F6.wireOp",EDGE,"E30.bottom"),sQuery(id+"F6.wireOp",EDGE,"E30.top"),sQuery(id+"F6.wireOp",EDGE,"E31.trimOffspring"),sQuery(id+"F6.wireOp",EDGE,"E32.trimOffspring")])],"isStart":true});var subQ4=makeQuery(id+"F1.opExtrude","SWEPT_FACE",FACE,{"disambiguationData":[OSD([subQ2])]});Q0=makeQuery(id+"F8.opChamfer","BLEND_EDGE",EDGE,{"blendedFrom":[makeQuery(id+"F7.boolean.opBoolean","INTERSECT",EDGE,{"derivedFrom":[subQ4,subQ3]}),makeQuery(id+"F7.boolean.opBoolean","SPLIT",FACE,{"disambiguationData":[TD([subQ3])],"derivedFrom":subQ4})],"blendedInto":[makeQuery(id+"F7.boolean.opBoolean","SPLIT",FACE,{"disambiguationData":[TD([subQ3])],"derivedFrom":subQ4})]});}
            var Q1;
            {var subQ2=sQuery(id+"F0.wireOp",EDGE,"E1");var subQ3=makeQuery(id+"F7.opExtrude","CAP_FACE",FACE,{"disambiguationData":[OSD([sQuery(id+"F6.wireOp",EDGE,"E25.bottom"),sQuery(id+"F6.wireOp",EDGE,"E25.top"),sQuery(id+"F6.wireOp",EDGE,"E25.left"),sQuery(id+"F6.wireOp",EDGE,"E25.right"),sQuery(id+"F6.wireOp",EDGE,"E26.MirrorCS"),sQuery(id+"F6.wireOp",EDGE,"E27.MirrorCS"),sQuery(id+"F6.wireOp",EDGE,"E28.MirrorCS"),sQuery(id+"F6.wireOp",EDGE,"E29.MirrorCS"),sQuery(id+"F6.wireOp",EDGE,"E30.bottom"),sQuery(id+"F6.wireOp",EDGE,"E30.top"),sQuery(id+"F6.wireOp",EDGE,"E31.trimOffspring"),sQuery(id+"F6.wireOp",EDGE,"E32.trimOffspring")])],"isStart":false});var subQ4=makeQuery(id+"F1.opExtrude","SWEPT_FACE",FACE,{"disambiguationData":[OSD([subQ2])]});Q1=makeQuery(id+"F8.opChamfer","BLEND_EDGE",EDGE,{"blendedFrom":[makeQuery(id+"F7.boolean.opBoolean","INTERSECT",EDGE,{"derivedFrom":[subQ4,subQ3]}),makeQuery(id+"F7.boolean.opBoolean","SPLIT",FACE,{"disambiguationData":[TD([subQ3])],"derivedFrom":subQ4})],"blendedInto":[makeQuery(id+"F7.boolean.opBoolean","SPLIT",FACE,{"disambiguationData":[TD([subQ3])],"derivedFrom":subQ4})]});}
            var Q2;
            {var subQ1=sQuery(id+"F0.wireOp",EDGE,"E9.MirrorCS");var subQ3=makeQuery(id+"F7.opExtrude","CAP_FACE",FACE,{"disambiguationData":[OSD([sQuery(id+"F6.wireOp",EDGE,"E25.bottom"),sQuery(id+"F6.wireOp",EDGE,"E25.top"),sQuery(id+"F6.wireOp",EDGE,"E25.left"),sQuery(id+"F6.wireOp",EDGE,"E25.right"),sQuery(id+"F6.wireOp",EDGE,"E26.MirrorCS"),sQuery(id+"F6.wireOp",EDGE,"E27.MirrorCS"),sQuery(id+"F6.wireOp",EDGE,"E28.MirrorCS"),sQuery(id+"F6.wireOp",EDGE,"E29.MirrorCS"),sQuery(id+"F6.wireOp",EDGE,"E30.bottom"),sQuery(id+"F6.wireOp",EDGE,"E30.top"),sQuery(id+"F6.wireOp",EDGE,"E31.trimOffspring"),sQuery(id+"F6.wireOp",EDGE,"E32.trimOffspring")])],"isStart":false});var subQ4=makeQuery(id+"F1.opExtrude","SWEPT_FACE",FACE,{"disambiguationData":[OSD([subQ1])]});Q2=makeQuery(id+"F8.opChamfer","BLEND_EDGE",EDGE,{"blendedFrom":[makeQuery(id+"F7.boolean.opBoolean","INTERSECT",EDGE,{"derivedFrom":[subQ4,subQ3]}),makeQuery(id+"F7.boolean.opBoolean","SPLIT",FACE,{"disambiguationData":[TD([subQ3])],"derivedFrom":subQ4})],"blendedInto":[makeQuery(id+"F7.boolean.opBoolean","SPLIT",FACE,{"disambiguationData":[TD([subQ3])],"derivedFrom":subQ4})]});}
            var Q3;
            {var subQ1=sQuery(id+"F0.wireOp",EDGE,"E9.MirrorCS");var subQ3=makeQuery(id+"F7.opExtrude","CAP_FACE",FACE,{"disambiguationData":[OSD([sQuery(id+"F6.wireOp",EDGE,"E25.bottom"),sQuery(id+"F6.wireOp",EDGE,"E25.top"),sQuery(id+"F6.wireOp",EDGE,"E25.left"),sQuery(id+"F6.wireOp",EDGE,"E25.right"),sQuery(id+"F6.wireOp",EDGE,"E26.MirrorCS"),sQuery(id+"F6.wireOp",EDGE,"E27.MirrorCS"),sQuery(id+"F6.wireOp",EDGE,"E28.MirrorCS"),sQuery(id+"F6.wireOp",EDGE,"E29.MirrorCS"),sQuery(id+"F6.wireOp",EDGE,"E30.bottom"),sQuery(id+"F6.wireOp",EDGE,"E30.top"),sQuery(id+"F6.wireOp",EDGE,"E31.trimOffspring"),sQuery(id+"F6.wireOp",EDGE,"E32.trimOffspring")])],"isStart":true});var subQ4=makeQuery(id+"F1.opExtrude","SWEPT_FACE",FACE,{"disambiguationData":[OSD([subQ1])]});Q3=makeQuery(id+"F8.opChamfer","BLEND_EDGE",EDGE,{"blendedFrom":[makeQuery(id+"F7.boolean.opBoolean","INTERSECT",EDGE,{"derivedFrom":[subQ4,subQ3]}),makeQuery(id+"F7.boolean.opBoolean","SPLIT",FACE,{"disambiguationData":[TD([subQ3])],"derivedFrom":subQ4})],"blendedInto":[makeQuery(id+"F7.boolean.opBoolean","SPLIT",FACE,{"disambiguationData":[TD([subQ3])],"derivedFrom":subQ4})]});}
            var Q4;
            {var subQ0=sQuery(id+"F0.wireOp",EDGE,"E9.MirrorCS");var subQ1=sQuery(id+"F0.wireOp",EDGE,"E7.MirrorCS");Q4=makeQuery(id+"F7.boolean.opBoolean","SPLIT",EDGE,{"disambiguationData":[TD([makeQuery(id+"F7.opExtrude","CAP_FACE",FACE,{"disambiguationData":[OSD([sQuery(id+"F6.wireOp",EDGE,"E25.bottom"),sQuery(id+"F6.wireOp",EDGE,"E25.top"),sQuery(id+"F6.wireOp",EDGE,"E25.left"),sQuery(id+"F6.wireOp",EDGE,"E25.right"),sQuery(id+"F6.wireOp",EDGE,"E26.MirrorCS"),sQuery(id+"F6.wireOp",EDGE,"E27.MirrorCS"),sQuery(id+"F6.wireOp",EDGE,"E28.MirrorCS"),sQuery(id+"F6.wireOp",EDGE,"E29.MirrorCS"),sQuery(id+"F6.wireOp",EDGE,"E30.bottom"),sQuery(id+"F6.wireOp",EDGE,"E30.top"),sQuery(id+"F6.wireOp",EDGE,"E31.trimOffspring"),sQuery(id+"F6.wireOp",EDGE,"E32.trimOffspring")])],"isStart":true})])],"derivedFrom":makeQuery(id+"F1.opExtrude","SWEPT_EDGE",EDGE,{"disambiguationData":[OSD([subQ1,subQ0])]})});}
            var Q5;
            {var subQ0=sQuery(id+"F0.wireOp",EDGE,"E0");var subQ1=sQuery(id+"F0.wireOp",EDGE,"E7.MirrorCS");Q5=makeQuery(id+"F7.boolean.opBoolean","SPLIT",EDGE,{"disambiguationData":[TD([makeQuery(id+"F7.opExtrude","CAP_FACE",FACE,{"disambiguationData":[OSD([sQuery(id+"F6.wireOp",EDGE,"E25.bottom"),sQuery(id+"F6.wireOp",EDGE,"E25.top"),sQuery(id+"F6.wireOp",EDGE,"E25.left"),sQuery(id+"F6.wireOp",EDGE,"E25.right"),sQuery(id+"F6.wireOp",EDGE,"E26.MirrorCS"),sQuery(id+"F6.wireOp",EDGE,"E27.MirrorCS"),sQuery(id+"F6.wireOp",EDGE,"E28.MirrorCS"),sQuery(id+"F6.wireOp",EDGE,"E29.MirrorCS"),sQuery(id+"F6.wireOp",EDGE,"E30.bottom"),sQuery(id+"F6.wireOp",EDGE,"E30.top"),sQuery(id+"F6.wireOp",EDGE,"E31.trimOffspring"),sQuery(id+"F6.wireOp",EDGE,"E32.trimOffspring")])],"isStart":true})])],"derivedFrom":makeQuery(id+"F1.opExtrude","SWEPT_EDGE",EDGE,{"disambiguationData":[OSD([subQ0,subQ1])]})});}
            var Q6;
            {var subQ0=sQuery(id+"F0.wireOp",EDGE,"E0");var subQ1=sQuery(id+"F0.wireOp",EDGE,"E7.MirrorCS");Q6=makeQuery(id+"F7.boolean.opBoolean","SPLIT",EDGE,{"disambiguationData":[TD([makeQuery(id+"F7.opExtrude","CAP_FACE",FACE,{"disambiguationData":[OSD([sQuery(id+"F6.wireOp",EDGE,"E25.bottom"),sQuery(id+"F6.wireOp",EDGE,"E25.top"),sQuery(id+"F6.wireOp",EDGE,"E25.left"),sQuery(id+"F6.wireOp",EDGE,"E25.right"),sQuery(id+"F6.wireOp",EDGE,"E26.MirrorCS"),sQuery(id+"F6.wireOp",EDGE,"E27.MirrorCS"),sQuery(id+"F6.wireOp",EDGE,"E28.MirrorCS"),sQuery(id+"F6.wireOp",EDGE,"E29.MirrorCS"),sQuery(id+"F6.wireOp",EDGE,"E30.bottom"),sQuery(id+"F6.wireOp",EDGE,"E30.top"),sQuery(id+"F6.wireOp",EDGE,"E31.trimOffspring"),sQuery(id+"F6.wireOp",EDGE,"E32.trimOffspring")])],"isStart":false})])],"derivedFrom":makeQuery(id+"F1.opExtrude","SWEPT_EDGE",EDGE,{"disambiguationData":[OSD([subQ0,subQ1])]})});}
            var Q7;
            {var subQ0=sQuery(id+"F0.wireOp",EDGE,"E9.MirrorCS");var subQ1=sQuery(id+"F0.wireOp",EDGE,"E7.MirrorCS");Q7=makeQuery(id+"F7.boolean.opBoolean","SPLIT",EDGE,{"disambiguationData":[TD([makeQuery(id+"F7.opExtrude","CAP_FACE",FACE,{"disambiguationData":[OSD([sQuery(id+"F6.wireOp",EDGE,"E25.bottom"),sQuery(id+"F6.wireOp",EDGE,"E25.top"),sQuery(id+"F6.wireOp",EDGE,"E25.left"),sQuery(id+"F6.wireOp",EDGE,"E25.right"),sQuery(id+"F6.wireOp",EDGE,"E26.MirrorCS"),sQuery(id+"F6.wireOp",EDGE,"E27.MirrorCS"),sQuery(id+"F6.wireOp",EDGE,"E28.MirrorCS"),sQuery(id+"F6.wireOp",EDGE,"E29.MirrorCS"),sQuery(id+"F6.wireOp",EDGE,"E30.bottom"),sQuery(id+"F6.wireOp",EDGE,"E30.top"),sQuery(id+"F6.wireOp",EDGE,"E31.trimOffspring"),sQuery(id+"F6.wireOp",EDGE,"E32.trimOffspring")])],"isStart":false})])],"derivedFrom":makeQuery(id+"F1.opExtrude","SWEPT_EDGE",EDGE,{"disambiguationData":[OSD([subQ1,subQ0])]})});}
            var Q8;
            {var subQ0=sQuery(id+"F0.wireOp",EDGE,"E5");var subQ1=sQuery(id+"F0.wireOp",EDGE,"E1");Q8=makeQuery(id+"F7.boolean.opBoolean","SPLIT",EDGE,{"disambiguationData":[TD([makeQuery(id+"F7.opExtrude","CAP_FACE",FACE,{"disambiguationData":[OSD([sQuery(id+"F6.wireOp",EDGE,"E25.bottom"),sQuery(id+"F6.wireOp",EDGE,"E25.top"),sQuery(id+"F6.wireOp",EDGE,"E25.left"),sQuery(id+"F6.wireOp",EDGE,"E25.right"),sQuery(id+"F6.wireOp",EDGE,"E26.MirrorCS"),sQuery(id+"F6.wireOp",EDGE,"E27.MirrorCS"),sQuery(id+"F6.wireOp",EDGE,"E28.MirrorCS"),sQuery(id+"F6.wireOp",EDGE,"E29.MirrorCS"),sQuery(id+"F6.wireOp",EDGE,"E30.bottom"),sQuery(id+"F6.wireOp",EDGE,"E30.top"),sQuery(id+"F6.wireOp",EDGE,"E31.trimOffspring"),sQuery(id+"F6.wireOp",EDGE,"E32.trimOffspring")])],"isStart":false})])],"derivedFrom":makeQuery(id+"F1.opExtrude","SWEPT_EDGE",EDGE,{"disambiguationData":[OSD([subQ1,subQ0])]})});}
            var Q9;
            {var subQ1=sQuery(id+"F0.wireOp",EDGE,"E5");Q9=makeQuery(id+"F18.opFillet","BLEND_EDGE",EDGE,{"blendedFrom":[makeQuery(id+"F10.opExtrude","TWEAK_EDGE",EDGE,{"derivedFrom":[makeQuery(id+"F9.imprint","IMPRINT",EDGE,{"derivedFrom":sQuery(id+"F9.wireOp",EDGE,"E40.0")}),makeQuery(id+"F9.imprint","IMPRINT",EDGE,{"derivedFrom":sQuery(id+"F9.wireOp",EDGE,"E41")})]}),makeQuery(id+"F7.boolean.opBoolean","SPLIT",FACE,{"disambiguationData":[TD([makeQuery(id+"F7.opExtrude","CAP_FACE",FACE,{"disambiguationData":[OSD([sQuery(id+"F6.wireOp",EDGE,"E25.bottom"),sQuery(id+"F6.wireOp",EDGE,"E25.top"),sQuery(id+"F6.wireOp",EDGE,"E25.left"),sQuery(id+"F6.wireOp",EDGE,"E25.right"),sQuery(id+"F6.wireOp",EDGE,"E26.MirrorCS"),sQuery(id+"F6.wireOp",EDGE,"E27.MirrorCS"),sQuery(id+"F6.wireOp",EDGE,"E28.MirrorCS"),sQuery(id+"F6.wireOp",EDGE,"E29.MirrorCS"),sQuery(id+"F6.wireOp",EDGE,"E30.bottom"),sQuery(id+"F6.wireOp",EDGE,"E30.top"),sQuery(id+"F6.wireOp",EDGE,"E31.trimOffspring"),sQuery(id+"F6.wireOp",EDGE,"E32.trimOffspring")])],"isStart":false})])],"derivedFrom":makeQuery(id+"F1.opExtrude","SWEPT_FACE",FACE,{"disambiguationData":[OSD([subQ1])]})})],"blendedInto":[makeQuery(id+"F7.boolean.opBoolean","SPLIT",FACE,{"disambiguationData":[TD([makeQuery(id+"F7.opExtrude","CAP_FACE",FACE,{"disambiguationData":[OSD([sQuery(id+"F6.wireOp",EDGE,"E25.bottom"),sQuery(id+"F6.wireOp",EDGE,"E25.top"),sQuery(id+"F6.wireOp",EDGE,"E25.left"),sQuery(id+"F6.wireOp",EDGE,"E25.right"),sQuery(id+"F6.wireOp",EDGE,"E26.MirrorCS"),sQuery(id+"F6.wireOp",EDGE,"E27.MirrorCS"),sQuery(id+"F6.wireOp",EDGE,"E28.MirrorCS"),sQuery(id+"F6.wireOp",EDGE,"E29.MirrorCS"),sQuery(id+"F6.wireOp",EDGE,"E30.bottom"),sQuery(id+"F6.wireOp",EDGE,"E30.top"),sQuery(id+"F6.wireOp",EDGE,"E31.trimOffspring"),sQuery(id+"F6.wireOp",EDGE,"E32.trimOffspring")])],"isStart":false})])],"derivedFrom":makeQuery(id+"F1.opExtrude","SWEPT_FACE",FACE,{"disambiguationData":[OSD([subQ1])]})})]});}
            var Q10;
            {var subQ1=sQuery(id+"F0.wireOp",EDGE,"E5");Q10=makeQuery(id+"F18.opFillet","BLEND_EDGE",EDGE,{"blendedFrom":[makeQuery(id+"F10.opExtrude","TWEAK_EDGE",EDGE,{"derivedFrom":[makeQuery(id+"F9.imprint","IMPRINT",EDGE,{"derivedFrom":sQuery(id+"F9.wireOp",EDGE,"E40.0")}),makeQuery(id+"F9.imprint","IMPRINT",EDGE,{"derivedFrom":sQuery(id+"F9.wireOp",EDGE,"E41")})]}),makeQuery(id+"F7.boolean.opBoolean","SPLIT",FACE,{"disambiguationData":[TD([makeQuery(id+"F7.opExtrude","CAP_FACE",FACE,{"disambiguationData":[OSD([sQuery(id+"F6.wireOp",EDGE,"E25.bottom"),sQuery(id+"F6.wireOp",EDGE,"E25.top"),sQuery(id+"F6.wireOp",EDGE,"E25.left"),sQuery(id+"F6.wireOp",EDGE,"E25.right"),sQuery(id+"F6.wireOp",EDGE,"E26.MirrorCS"),sQuery(id+"F6.wireOp",EDGE,"E27.MirrorCS"),sQuery(id+"F6.wireOp",EDGE,"E28.MirrorCS"),sQuery(id+"F6.wireOp",EDGE,"E29.MirrorCS"),sQuery(id+"F6.wireOp",EDGE,"E30.bottom"),sQuery(id+"F6.wireOp",EDGE,"E30.top"),sQuery(id+"F6.wireOp",EDGE,"E31.trimOffspring"),sQuery(id+"F6.wireOp",EDGE,"E32.trimOffspring")])],"isStart":true})])],"derivedFrom":makeQuery(id+"F1.opExtrude","SWEPT_FACE",FACE,{"disambiguationData":[OSD([subQ1])]})})],"blendedInto":[makeQuery(id+"F7.boolean.opBoolean","SPLIT",FACE,{"disambiguationData":[TD([makeQuery(id+"F7.opExtrude","CAP_FACE",FACE,{"disambiguationData":[OSD([sQuery(id+"F6.wireOp",EDGE,"E25.bottom"),sQuery(id+"F6.wireOp",EDGE,"E25.top"),sQuery(id+"F6.wireOp",EDGE,"E25.left"),sQuery(id+"F6.wireOp",EDGE,"E25.right"),sQuery(id+"F6.wireOp",EDGE,"E26.MirrorCS"),sQuery(id+"F6.wireOp",EDGE,"E27.MirrorCS"),sQuery(id+"F6.wireOp",EDGE,"E28.MirrorCS"),sQuery(id+"F6.wireOp",EDGE,"E29.MirrorCS"),sQuery(id+"F6.wireOp",EDGE,"E30.bottom"),sQuery(id+"F6.wireOp",EDGE,"E30.top"),sQuery(id+"F6.wireOp",EDGE,"E31.trimOffspring"),sQuery(id+"F6.wireOp",EDGE,"E32.trimOffspring")])],"isStart":true})])],"derivedFrom":makeQuery(id+"F1.opExtrude","SWEPT_FACE",FACE,{"disambiguationData":[OSD([subQ1])]})})]});}
            var Q11;
            {var subQ0=sQuery(id+"F0.wireOp",EDGE,"E5");var subQ1=sQuery(id+"F0.wireOp",EDGE,"E1");Q11=makeQuery(id+"F7.boolean.opBoolean","SPLIT",EDGE,{"disambiguationData":[TD([makeQuery(id+"F7.opExtrude","CAP_FACE",FACE,{"disambiguationData":[OSD([sQuery(id+"F6.wireOp",EDGE,"E25.bottom"),sQuery(id+"F6.wireOp",EDGE,"E25.top"),sQuery(id+"F6.wireOp",EDGE,"E25.left"),sQuery(id+"F6.wireOp",EDGE,"E25.right"),sQuery(id+"F6.wireOp",EDGE,"E26.MirrorCS"),sQuery(id+"F6.wireOp",EDGE,"E27.MirrorCS"),sQuery(id+"F6.wireOp",EDGE,"E28.MirrorCS"),sQuery(id+"F6.wireOp",EDGE,"E29.MirrorCS"),sQuery(id+"F6.wireOp",EDGE,"E30.bottom"),sQuery(id+"F6.wireOp",EDGE,"E30.top"),sQuery(id+"F6.wireOp",EDGE,"E31.trimOffspring"),sQuery(id+"F6.wireOp",EDGE,"E32.trimOffspring")])],"isStart":true})])],"derivedFrom":makeQuery(id+"F1.opExtrude","SWEPT_EDGE",EDGE,{"disambiguationData":[OSD([subQ1,subQ0])]})});}
            var Q12;
            {var subQ0=sQuery(id+"F0.wireOp",EDGE,"E20.MirrorCS");Q12=makeQuery(id+"F10.boolean.opBoolean","INTERSECT",EDGE,{"derivedFrom":[makeQuery(id+"F7.boolean.opBoolean","SPLIT",FACE,{"disambiguationData":[TD([makeQuery(id+"F7.opExtrude","CAP_FACE",FACE,{"disambiguationData":[OSD([sQuery(id+"F6.wireOp",EDGE,"E25.bottom"),sQuery(id+"F6.wireOp",EDGE,"E25.top"),sQuery(id+"F6.wireOp",EDGE,"E25.left"),sQuery(id+"F6.wireOp",EDGE,"E25.right"),sQuery(id+"F6.wireOp",EDGE,"E26.MirrorCS"),sQuery(id+"F6.wireOp",EDGE,"E27.MirrorCS"),sQuery(id+"F6.wireOp",EDGE,"E28.MirrorCS"),sQuery(id+"F6.wireOp",EDGE,"E29.MirrorCS"),sQuery(id+"F6.wireOp",EDGE,"E30.bottom"),sQuery(id+"F6.wireOp",EDGE,"E30.top"),sQuery(id+"F6.wireOp",EDGE,"E31.trimOffspring"),sQuery(id+"F6.wireOp",EDGE,"E32.trimOffspring")])],"isStart":true})])],"derivedFrom":makeQuery(id+"F1.opExtrude","SWEPT_FACE",FACE,{"disambiguationData":[OSD([subQ0])]})}),makeQuery(id+"F10.opExtrude","SWEPT_FACE",FACE,{"disambiguationData":[OSD([sQuery(id+"F9.wireOp",EDGE,"E40.0")])]})]});}
            var Q13;
            {var subQ0=sQuery(id+"F0.wireOp",EDGE,"E20.MirrorCS");var subQ1=sQuery(id+"F0.wireOp",EDGE,"E19.MirrorCS");Q13=makeQuery(id+"F7.boolean.opBoolean","SPLIT",EDGE,{"disambiguationData":[TD([makeQuery(id+"F7.opExtrude","CAP_FACE",FACE,{"disambiguationData":[OSD([sQuery(id+"F6.wireOp",EDGE,"E25.bottom"),sQuery(id+"F6.wireOp",EDGE,"E25.top"),sQuery(id+"F6.wireOp",EDGE,"E25.left"),sQuery(id+"F6.wireOp",EDGE,"E25.right"),sQuery(id+"F6.wireOp",EDGE,"E26.MirrorCS"),sQuery(id+"F6.wireOp",EDGE,"E27.MirrorCS"),sQuery(id+"F6.wireOp",EDGE,"E28.MirrorCS"),sQuery(id+"F6.wireOp",EDGE,"E29.MirrorCS"),sQuery(id+"F6.wireOp",EDGE,"E30.bottom"),sQuery(id+"F6.wireOp",EDGE,"E30.top"),sQuery(id+"F6.wireOp",EDGE,"E31.trimOffspring"),sQuery(id+"F6.wireOp",EDGE,"E32.trimOffspring")])],"isStart":true})])],"derivedFrom":makeQuery(id+"F1.opExtrude","SWEPT_EDGE",EDGE,{"disambiguationData":[OSD([subQ1,subQ0])]})});}
            var Q14;
            {var subQ0=sQuery(id+"F0.wireOp",EDGE,"E20.MirrorCS");Q14=makeQuery(id+"F10.boolean.opBoolean","INTERSECT",EDGE,{"derivedFrom":[makeQuery(id+"F7.boolean.opBoolean","SPLIT",FACE,{"disambiguationData":[TD([makeQuery(id+"F7.opExtrude","CAP_FACE",FACE,{"disambiguationData":[OSD([sQuery(id+"F6.wireOp",EDGE,"E25.bottom"),sQuery(id+"F6.wireOp",EDGE,"E25.top"),sQuery(id+"F6.wireOp",EDGE,"E25.left"),sQuery(id+"F6.wireOp",EDGE,"E25.right"),sQuery(id+"F6.wireOp",EDGE,"E26.MirrorCS"),sQuery(id+"F6.wireOp",EDGE,"E27.MirrorCS"),sQuery(id+"F6.wireOp",EDGE,"E28.MirrorCS"),sQuery(id+"F6.wireOp",EDGE,"E29.MirrorCS"),sQuery(id+"F6.wireOp",EDGE,"E30.bottom"),sQuery(id+"F6.wireOp",EDGE,"E30.top"),sQuery(id+"F6.wireOp",EDGE,"E31.trimOffspring"),sQuery(id+"F6.wireOp",EDGE,"E32.trimOffspring")])],"isStart":false})])],"derivedFrom":makeQuery(id+"F1.opExtrude","SWEPT_FACE",FACE,{"disambiguationData":[OSD([subQ0])]})}),makeQuery(id+"F10.opExtrude","SWEPT_FACE",FACE,{"disambiguationData":[OSD([sQuery(id+"F9.wireOp",EDGE,"E40.0")])]})]});}
            var Q15;
            {var subQ0=sQuery(id+"F0.wireOp",EDGE,"E20.MirrorCS");var subQ1=sQuery(id+"F0.wireOp",EDGE,"E19.MirrorCS");Q15=makeQuery(id+"F7.boolean.opBoolean","SPLIT",EDGE,{"disambiguationData":[TD([makeQuery(id+"F7.opExtrude","CAP_FACE",FACE,{"disambiguationData":[OSD([sQuery(id+"F6.wireOp",EDGE,"E25.bottom"),sQuery(id+"F6.wireOp",EDGE,"E25.top"),sQuery(id+"F6.wireOp",EDGE,"E25.left"),sQuery(id+"F6.wireOp",EDGE,"E25.right"),sQuery(id+"F6.wireOp",EDGE,"E26.MirrorCS"),sQuery(id+"F6.wireOp",EDGE,"E27.MirrorCS"),sQuery(id+"F6.wireOp",EDGE,"E28.MirrorCS"),sQuery(id+"F6.wireOp",EDGE,"E29.MirrorCS"),sQuery(id+"F6.wireOp",EDGE,"E30.bottom"),sQuery(id+"F6.wireOp",EDGE,"E30.top"),sQuery(id+"F6.wireOp",EDGE,"E31.trimOffspring"),sQuery(id+"F6.wireOp",EDGE,"E32.trimOffspring")])],"isStart":false})])],"derivedFrom":makeQuery(id+"F1.opExtrude","SWEPT_EDGE",EDGE,{"disambiguationData":[OSD([subQ1,subQ0])]})});}
            var Q16;
            {var subQ1=sQuery(id+"F0.wireOp",EDGE,"E19.MirrorCS");var subQ3=makeQuery(id+"F7.opExtrude","CAP_FACE",FACE,{"disambiguationData":[OSD([sQuery(id+"F6.wireOp",EDGE,"E25.bottom"),sQuery(id+"F6.wireOp",EDGE,"E25.top"),sQuery(id+"F6.wireOp",EDGE,"E25.left"),sQuery(id+"F6.wireOp",EDGE,"E25.right"),sQuery(id+"F6.wireOp",EDGE,"E26.MirrorCS"),sQuery(id+"F6.wireOp",EDGE,"E27.MirrorCS"),sQuery(id+"F6.wireOp",EDGE,"E28.MirrorCS"),sQuery(id+"F6.wireOp",EDGE,"E29.MirrorCS"),sQuery(id+"F6.wireOp",EDGE,"E30.bottom"),sQuery(id+"F6.wireOp",EDGE,"E30.top"),sQuery(id+"F6.wireOp",EDGE,"E31.trimOffspring"),sQuery(id+"F6.wireOp",EDGE,"E32.trimOffspring")])],"isStart":true});var subQ4=makeQuery(id+"F1.opExtrude","SWEPT_FACE",FACE,{"disambiguationData":[OSD([subQ1])]});Q16=makeQuery(id+"F8.opChamfer","BLEND_EDGE",EDGE,{"blendedFrom":[makeQuery(id+"F7.boolean.opBoolean","INTERSECT",EDGE,{"derivedFrom":[subQ4,subQ3]}),makeQuery(id+"F7.boolean.opBoolean","SPLIT",FACE,{"disambiguationData":[TD([subQ3])],"derivedFrom":subQ4})],"blendedInto":[makeQuery(id+"F7.boolean.opBoolean","SPLIT",FACE,{"disambiguationData":[TD([subQ3])],"derivedFrom":subQ4})]});}
            var Q17;
            {var subQ1=sQuery(id+"F0.wireOp",EDGE,"E19.MirrorCS");var subQ3=makeQuery(id+"F7.opExtrude","CAP_FACE",FACE,{"disambiguationData":[OSD([sQuery(id+"F6.wireOp",EDGE,"E25.bottom"),sQuery(id+"F6.wireOp",EDGE,"E25.top"),sQuery(id+"F6.wireOp",EDGE,"E25.left"),sQuery(id+"F6.wireOp",EDGE,"E25.right"),sQuery(id+"F6.wireOp",EDGE,"E26.MirrorCS"),sQuery(id+"F6.wireOp",EDGE,"E27.MirrorCS"),sQuery(id+"F6.wireOp",EDGE,"E28.MirrorCS"),sQuery(id+"F6.wireOp",EDGE,"E29.MirrorCS"),sQuery(id+"F6.wireOp",EDGE,"E30.bottom"),sQuery(id+"F6.wireOp",EDGE,"E30.top"),sQuery(id+"F6.wireOp",EDGE,"E31.trimOffspring"),sQuery(id+"F6.wireOp",EDGE,"E32.trimOffspring")])],"isStart":false});var subQ4=makeQuery(id+"F1.opExtrude","SWEPT_FACE",FACE,{"disambiguationData":[OSD([subQ1])]});Q17=makeQuery(id+"F8.opChamfer","BLEND_EDGE",EDGE,{"blendedFrom":[makeQuery(id+"F7.boolean.opBoolean","INTERSECT",EDGE,{"derivedFrom":[subQ4,subQ3]}),makeQuery(id+"F7.boolean.opBoolean","SPLIT",FACE,{"disambiguationData":[TD([subQ3])],"derivedFrom":subQ4})],"blendedInto":[makeQuery(id+"F7.boolean.opBoolean","SPLIT",FACE,{"disambiguationData":[TD([subQ3])],"derivedFrom":subQ4})]});}
            var Q18;
            Q18=makeQuery(id+"F10.opExtrude","TWEAK_EDGE",EDGE,{"derivedFrom":[makeQuery(id+"F9.imprint","IMPRINT",EDGE,{"derivedFrom":sQuery(id+"F9.wireOp",EDGE,"E40.0")}),makeQuery(id+"F9.imprint","IMPRINT",EDGE,{"derivedFrom":sQuery(id+"F9.wireOp",EDGE,"E40.4")})]});
            var Q19;
            Q19=makeQuery(id+"F10.opExtrude","TWEAK_EDGE",EDGE,{"derivedFrom":[makeQuery(id+"F9.imprint","IMPRINT",EDGE,{"derivedFrom":sQuery(id+"F9.wireOp",EDGE,"E40.3")}),makeQuery(id+"F9.imprint","IMPRINT",EDGE,{"derivedFrom":sQuery(id+"F9.wireOp",EDGE,"E40.4")})]});
            var Q20;
            {var subQ0=sQuery(id+"F0.wireOp",EDGE,"E16.MirrorCS");var subQ1=sQuery(id+"F0.wireOp",EDGE,"E14.MirrorCS");Q20=makeQuery(id+"F7.boolean.opBoolean","SPLIT",EDGE,{"disambiguationData":[TD([makeQuery(id+"F7.opExtrude","CAP_FACE",FACE,{"disambiguationData":[OSD([sQuery(id+"F6.wireOp",EDGE,"E25.bottom"),sQuery(id+"F6.wireOp",EDGE,"E25.top"),sQuery(id+"F6.wireOp",EDGE,"E25.left"),sQuery(id+"F6.wireOp",EDGE,"E25.right"),sQuery(id+"F6.wireOp",EDGE,"E26.MirrorCS"),sQuery(id+"F6.wireOp",EDGE,"E27.MirrorCS"),sQuery(id+"F6.wireOp",EDGE,"E28.MirrorCS"),sQuery(id+"F6.wireOp",EDGE,"E29.MirrorCS"),sQuery(id+"F6.wireOp",EDGE,"E30.bottom"),sQuery(id+"F6.wireOp",EDGE,"E30.top"),sQuery(id+"F6.wireOp",EDGE,"E31.trimOffspring"),sQuery(id+"F6.wireOp",EDGE,"E32.trimOffspring")])],"isStart":false})])],"derivedFrom":makeQuery(id+"F1.opExtrude","SWEPT_EDGE",EDGE,{"disambiguationData":[OSD([subQ1,subQ0])]})});}
            var Q21;
            {var subQ1=sQuery(id+"F0.wireOp",EDGE,"E14.MirrorCS");var subQ3=makeQuery(id+"F7.opExtrude","CAP_FACE",FACE,{"disambiguationData":[OSD([sQuery(id+"F6.wireOp",EDGE,"E25.bottom"),sQuery(id+"F6.wireOp",EDGE,"E25.top"),sQuery(id+"F6.wireOp",EDGE,"E25.left"),sQuery(id+"F6.wireOp",EDGE,"E25.right"),sQuery(id+"F6.wireOp",EDGE,"E26.MirrorCS"),sQuery(id+"F6.wireOp",EDGE,"E27.MirrorCS"),sQuery(id+"F6.wireOp",EDGE,"E28.MirrorCS"),sQuery(id+"F6.wireOp",EDGE,"E29.MirrorCS"),sQuery(id+"F6.wireOp",EDGE,"E30.bottom"),sQuery(id+"F6.wireOp",EDGE,"E30.top"),sQuery(id+"F6.wireOp",EDGE,"E31.trimOffspring"),sQuery(id+"F6.wireOp",EDGE,"E32.trimOffspring")])],"isStart":false});var subQ4=makeQuery(id+"F1.opExtrude","SWEPT_FACE",FACE,{"disambiguationData":[OSD([subQ1])]});Q21=makeQuery(id+"F8.opChamfer","BLEND_EDGE",EDGE,{"blendedFrom":[makeQuery(id+"F7.boolean.opBoolean","INTERSECT",EDGE,{"derivedFrom":[subQ4,subQ3]}),makeQuery(id+"F7.boolean.opBoolean","SPLIT",FACE,{"disambiguationData":[TD([subQ3])],"derivedFrom":subQ4})],"blendedInto":[makeQuery(id+"F7.boolean.opBoolean","SPLIT",FACE,{"disambiguationData":[TD([subQ3])],"derivedFrom":subQ4})]});}
            var Q22;
            {var subQ1=sQuery(id+"F0.wireOp",EDGE,"E14.MirrorCS");var subQ3=makeQuery(id+"F7.opExtrude","CAP_FACE",FACE,{"disambiguationData":[OSD([sQuery(id+"F6.wireOp",EDGE,"E25.bottom"),sQuery(id+"F6.wireOp",EDGE,"E25.top"),sQuery(id+"F6.wireOp",EDGE,"E25.left"),sQuery(id+"F6.wireOp",EDGE,"E25.right"),sQuery(id+"F6.wireOp",EDGE,"E26.MirrorCS"),sQuery(id+"F6.wireOp",EDGE,"E27.MirrorCS"),sQuery(id+"F6.wireOp",EDGE,"E28.MirrorCS"),sQuery(id+"F6.wireOp",EDGE,"E29.MirrorCS"),sQuery(id+"F6.wireOp",EDGE,"E30.bottom"),sQuery(id+"F6.wireOp",EDGE,"E30.top"),sQuery(id+"F6.wireOp",EDGE,"E31.trimOffspring"),sQuery(id+"F6.wireOp",EDGE,"E32.trimOffspring")])],"isStart":true});var subQ4=makeQuery(id+"F1.opExtrude","SWEPT_FACE",FACE,{"disambiguationData":[OSD([subQ1])]});Q22=makeQuery(id+"F8.opChamfer","BLEND_EDGE",EDGE,{"blendedFrom":[makeQuery(id+"F7.boolean.opBoolean","INTERSECT",EDGE,{"derivedFrom":[subQ4,subQ3]}),makeQuery(id+"F7.boolean.opBoolean","SPLIT",FACE,{"disambiguationData":[TD([subQ3])],"derivedFrom":subQ4})],"blendedInto":[makeQuery(id+"F7.boolean.opBoolean","SPLIT",FACE,{"disambiguationData":[TD([subQ3])],"derivedFrom":subQ4})]});}
            var Q23;
            {var subQ0=sQuery(id+"F0.wireOp",EDGE,"E16.MirrorCS");var subQ1=sQuery(id+"F0.wireOp",EDGE,"E14.MirrorCS");Q23=makeQuery(id+"F7.boolean.opBoolean","SPLIT",EDGE,{"disambiguationData":[TD([makeQuery(id+"F7.opExtrude","CAP_FACE",FACE,{"disambiguationData":[OSD([sQuery(id+"F6.wireOp",EDGE,"E25.bottom"),sQuery(id+"F6.wireOp",EDGE,"E25.top"),sQuery(id+"F6.wireOp",EDGE,"E25.left"),sQuery(id+"F6.wireOp",EDGE,"E25.right"),sQuery(id+"F6.wireOp",EDGE,"E26.MirrorCS"),sQuery(id+"F6.wireOp",EDGE,"E27.MirrorCS"),sQuery(id+"F6.wireOp",EDGE,"E28.MirrorCS"),sQuery(id+"F6.wireOp",EDGE,"E29.MirrorCS"),sQuery(id+"F6.wireOp",EDGE,"E30.bottom"),sQuery(id+"F6.wireOp",EDGE,"E30.top"),sQuery(id+"F6.wireOp",EDGE,"E31.trimOffspring"),sQuery(id+"F6.wireOp",EDGE,"E32.trimOffspring")])],"isStart":true})])],"derivedFrom":makeQuery(id+"F1.opExtrude","SWEPT_EDGE",EDGE,{"disambiguationData":[OSD([subQ1,subQ0])]})});}
            var Q24;
            Q24=makeQuery(id+"F10.opExtrude","TWEAK_EDGE",EDGE,{"derivedFrom":[makeQuery(id+"F9.imprint","IMPRINT",EDGE,{"derivedFrom":sQuery(id+"F9.wireOp",EDGE,"E40.2")}),makeQuery(id+"F9.imprint","IMPRINT",EDGE,{"derivedFrom":sQuery(id+"F9.wireOp",EDGE,"E40.3")}),makeQuery(id+"F9.imprint","IMPRINT",EDGE,{"derivedFrom":sQuery(id+"F9.wireOp",EDGE,"E42")})]});
            var Q25;
            {var subQ1=sQuery(id+"F0.wireOp",EDGE,"E16.MirrorCS");Q25=makeQuery(id+"F10.boolean.opBoolean","INTERSECT",EDGE,{"derivedFrom":[makeQuery(id+"F7.boolean.opBoolean","SPLIT",FACE,{"disambiguationData":[TD([makeQuery(id+"F7.opExtrude","CAP_FACE",FACE,{"disambiguationData":[OSD([sQuery(id+"F6.wireOp",EDGE,"E25.bottom"),sQuery(id+"F6.wireOp",EDGE,"E25.top"),sQuery(id+"F6.wireOp",EDGE,"E25.left"),sQuery(id+"F6.wireOp",EDGE,"E25.right"),sQuery(id+"F6.wireOp",EDGE,"E26.MirrorCS"),sQuery(id+"F6.wireOp",EDGE,"E27.MirrorCS"),sQuery(id+"F6.wireOp",EDGE,"E28.MirrorCS"),sQuery(id+"F6.wireOp",EDGE,"E29.MirrorCS"),sQuery(id+"F6.wireOp",EDGE,"E30.bottom"),sQuery(id+"F6.wireOp",EDGE,"E30.top"),sQuery(id+"F6.wireOp",EDGE,"E31.trimOffspring"),sQuery(id+"F6.wireOp",EDGE,"E32.trimOffspring")])],"isStart":false})])],"derivedFrom":makeQuery(id+"F1.opExtrude","SWEPT_FACE",FACE,{"disambiguationData":[OSD([subQ1])]})}),makeQuery(id+"F10.opExtrude","SWEPT_FACE",FACE,{"disambiguationData":[OSD([sQuery(id+"F9.wireOp",EDGE,"E40.2"),sQuery(id+"F9.wireOp",EDGE,"E42")])]})]});}
            var Q26;
            {var subQ1=sQuery(id+"F0.wireOp",EDGE,"E16.MirrorCS");Q26=makeQuery(id+"F10.boolean.opBoolean","INTERSECT",EDGE,{"derivedFrom":[makeQuery(id+"F7.boolean.opBoolean","SPLIT",FACE,{"disambiguationData":[TD([makeQuery(id+"F7.opExtrude","CAP_FACE",FACE,{"disambiguationData":[OSD([sQuery(id+"F6.wireOp",EDGE,"E25.bottom"),sQuery(id+"F6.wireOp",EDGE,"E25.top"),sQuery(id+"F6.wireOp",EDGE,"E25.left"),sQuery(id+"F6.wireOp",EDGE,"E25.right"),sQuery(id+"F6.wireOp",EDGE,"E26.MirrorCS"),sQuery(id+"F6.wireOp",EDGE,"E27.MirrorCS"),sQuery(id+"F6.wireOp",EDGE,"E28.MirrorCS"),sQuery(id+"F6.wireOp",EDGE,"E29.MirrorCS"),sQuery(id+"F6.wireOp",EDGE,"E30.bottom"),sQuery(id+"F6.wireOp",EDGE,"E30.top"),sQuery(id+"F6.wireOp",EDGE,"E31.trimOffspring"),sQuery(id+"F6.wireOp",EDGE,"E32.trimOffspring")])],"isStart":true})])],"derivedFrom":makeQuery(id+"F1.opExtrude","SWEPT_FACE",FACE,{"disambiguationData":[OSD([subQ1])]})}),makeQuery(id+"F10.opExtrude","SWEPT_FACE",FACE,{"disambiguationData":[OSD([sQuery(id+"F9.wireOp",EDGE,"E40.2"),sQuery(id+"F9.wireOp",EDGE,"E42")])]})]});}
            fillet(context, id + "F19", {"entities" : qUnion([Q0, Q1, Q2, Q3, Q4, Q5, Q6, Q7, Q8, Q9, Q10, Q11, Q12, Q13, Q14, Q15, Q16, Q17, Q18, Q19, Q20, Q21, Q22, Q23, Q24, Q25, Q26]), "radius" : 0.5 * mm, "tangentPropagation" : true, "allowEdgeOverflow" : false});
        }
        {
            var Q0;
            {var subQ21=sQuery(id+"F0.wireOp",EDGE,"E0");var subQ24=sQuery(id+"F6.wireOp",EDGE,"E32.trimOffspring");var subQ25=sQuery(id+"F6.wireOp",EDGE,"E31.trimOffspring");var subQ26=sQuery(id+"F6.wireOp",EDGE,"E30.top");var subQ27=sQuery(id+"F6.wireOp",EDGE,"E30.bottom");var subQ28=sQuery(id+"F6.wireOp",EDGE,"E29.MirrorCS");var subQ29=sQuery(id+"F6.wireOp",EDGE,"E28.MirrorCS");var subQ30=sQuery(id+"F6.wireOp",EDGE,"E27.MirrorCS");var subQ31=sQuery(id+"F6.wireOp",EDGE,"E26.MirrorCS");var subQ32=sQuery(id+"F6.wireOp",EDGE,"E25.right");var subQ33=sQuery(id+"F6.wireOp",EDGE,"E25.left");var subQ34=sQuery(id+"F6.wireOp",EDGE,"E25.top");var subQ35=sQuery(id+"F6.wireOp",EDGE,"E25.bottom");var subQ36=makeQuery(id+"F1.opExtrude","SWEPT_FACE",FACE,{"disambiguationData":[OSD([subQ21])]});Q0=makeQuery(id+"F10.boolean.opBoolean","MERGE",FACE,{"derivedFrom":[makeQuery(id+"F7.boolean.opBoolean","SPLIT",FACE,{"disambiguationData":[TD([makeQuery(id+"F7.opExtrude","CAP_FACE",FACE,{"disambiguationData":[OSD([subQ35,subQ34,subQ33,subQ32,subQ31,subQ30,subQ29,subQ28,subQ27,subQ26,subQ25,subQ24])],"isStart":true})])],"derivedFrom":subQ36}),makeQuery(id+"F7.boolean.opBoolean","SPLIT",FACE,{"disambiguationData":[TD([makeQuery(id+"F7.opExtrude","CAP_FACE",FACE,{"disambiguationData":[OSD([subQ35,subQ34,subQ33,subQ32,subQ31,subQ30,subQ29,subQ28,subQ27,subQ26,subQ25,subQ24])],"isStart":false})])],"derivedFrom":subQ36}),makeQuery(id+"F10.opExtrude","SWEPT_FACE",FACE,{"disambiguationData":[OSD([sQuery(id+"F9.wireOp",EDGE,"E41")])]})]});}
            var sketch = newSketch(context, id + "F20", { "sketchPlane" : qUnion([Q0])});
            skLineSegment(sketch, "E46.bottom", {"start": v(-7, 25) * mm, "end": v(3, 25) * mm});
            skLineSegment(sketch, "E46.top", {"start": v(-7, 15) * mm, "end": v(3, 15) * mm});
            skLineSegment(sketch, "E46.left", {"start": v(-7, 25) * mm, "end": v(-7, 15) * mm});
            skLineSegment(sketch, "E46.right", {"start": v(3, 25) * mm, "end": v(3, 15) * mm});
            skLineSegment(sketch, "E47.bottom", {"start": v(-7, -25) * mm, "end": v(3, -25) * mm});
            skLineSegment(sketch, "E47.top", {"start": v(-7, -15) * mm, "end": v(3, -15) * mm});
            skLineSegment(sketch, "E47.left", {"start": v(-7, -25) * mm, "end": v(-7, -15) * mm});
            skLineSegment(sketch, "E47.right", {"start": v(3, -25) * mm, "end": v(3, -15) * mm});
            skSolve(sketch);
        }
        {
            var Q0;
            Q0 = qSketchRegion(id + "F20", true);
            extrude(context, id + "F21", {"entities" : qUnion([Q0]), "operationType" : NewBodyOperationType.REMOVE, "endBound" : BoundingType.THROUGH_ALL, "oppositeDirection" : true, "depth" : 25 * mm, "hasSecondDirection" : true, "secondDirectionBound" : BoundingType.THROUGH_ALL, "secondDirectionOppositeDirection" : false, "secondDirectionDepth" : 25 * mm});
        }
    });
